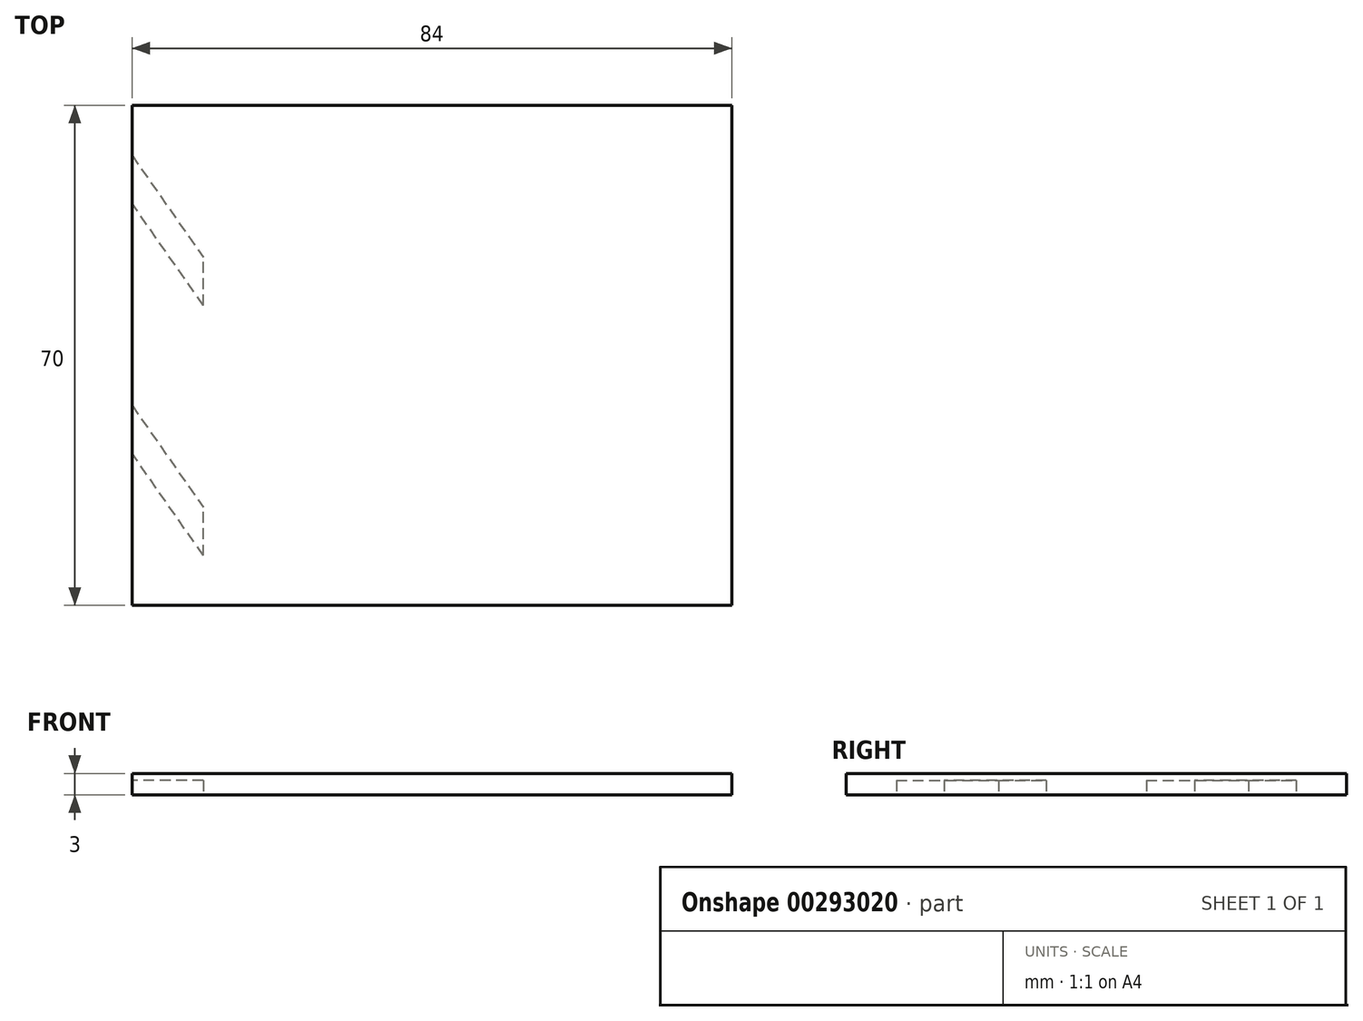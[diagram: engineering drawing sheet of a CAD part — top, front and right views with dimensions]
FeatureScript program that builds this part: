
annotation { "Feature Type Name" : "Feature", "Feature Type Description" : "" }
export const myFeature = defineFeature(function(context is Context, id is Id, definition is map)
    precondition{}
    {
        {
            var Q0;
            Q0=qCreatedBy(makeId("Front.planeOp"),FACE);
            var sketch = newSketch(context, id + "F0", { "sketchPlane" : qUnion([Q0])});
            skLineSegment(sketch, "E0.bottom", {"start": v(0, -23) * mm, "end": v(42, -23) * mm});
            skLineSegment(sketch, "E0.top", {"start": v(0, -20) * mm, "end": v(42, -20) * mm});
            skLineSegment(sketch, "E0.left", {"start": v(0, -23) * mm, "end": v(0, -20) * mm});
            skLineSegment(sketch, "E0.right", {"start": v(42, -23) * mm, "end": v(42, -20) * mm});
            skLineSegment(sketch, "E1", {"start": v(0, 0) * mm, "end": v(0, -20) * mm, "construction": true});
            skLineSegment(sketch, "E2", {"start": v(42, -21.5) * mm, "end": v(34, -21.5) * mm, "construction": true});
            skPoint(sketch, "E2.endSnap0", {"position": v(42, -21.5) * mm});
            skLineSegment(sketch, "E3", {"start": v(34, -21.5) * mm, "end": v(32, -21.5) * mm, "construction": true});
            skLineSegment(sketch, "E4", {"start": v(32, -21.5) * mm, "end": v(30, -21.5) * mm, "construction": true});
            skLineSegment(sketch, "E5", {"start": v(30, -21.5) * mm, "end": v(21, -21.5) * mm, "construction": true});
            skLineSegment(sketch, "E6", {"start": v(21, -21.5) * mm, "end": v(17, -21.5) * mm, "construction": true});
            skLineSegment(sketch, "E7", {"start": v(17, -21.5) * mm, "end": v(0, -21.5) * mm, "construction": true});
            skLineSegment(sketch, "E8", {"start": v(32, -21.5) * mm, "end": v(32, -23) * mm, "construction": true});
            skLineSegment(sketch, "E9", {"start": v(32, -23) * mm, "end": v(32, -21) * mm});
            skPoint(sketch, "E9.endSnap0", {"position": v(32, -22.25) * mm});
            skLineSegment(sketch, "E10", {"start": v(32, -21) * mm, "end": v(42, -21) * mm});
            skLineSegment(sketch, "E11", {"start": v(32, -22.25) * mm, "end": v(38, -22.25) * mm, "construction": true});
            skLineSegment(sketch, "E12", {"start": v(38, -22.25) * mm, "end": v(38, -23) * mm});
            skLineSegment(sketch, "E13", {"start": v(38, -23) * mm, "end": v(38, -21) * mm});
            skLineSegment(sketch, "E14.MirrorCS", {"start": v(-32, -23) * mm, "end": v(-32, -21) * mm});
            skLineSegment(sketch, "E15.MirrorCS", {"start": v(-32, -21.5) * mm, "end": v(-32, -23) * mm, "construction": true});
            skLineSegment(sketch, "E16.MirrorCS", {"start": v(-34, -21.5) * mm, "end": v(-32, -21.5) * mm, "construction": true});
            skLineSegment(sketch, "E17.MirrorCS", {"start": v(-32, -21.5) * mm, "end": v(-30, -21.5) * mm, "construction": true});
            skLineSegment(sketch, "E18.MirrorCS", {"start": v(-38, -23) * mm, "end": v(-38, -21) * mm});
            skLineSegment(sketch, "E19.MirrorCS", {"start": v(-38, -22.25) * mm, "end": v(-38, -23) * mm});
            skLineSegment(sketch, "E20.MirrorCS", {"start": v(-42, -23) * mm, "end": v(-42, -20) * mm});
            skLineSegment(sketch, "E21.MirrorCS", {"start": v(-42, -21.5) * mm, "end": v(-34, -21.5) * mm, "construction": true});
            skLineSegment(sketch, "E22.MirrorCS", {"start": v(-32, -21) * mm, "end": v(-42, -21) * mm});
            skLineSegment(sketch, "E23.MirrorCS", {"start": v(-32, -22.25) * mm, "end": v(-38, -22.25) * mm, "construction": true});
            skPoint(sketch, "E24.MirrorP", {"position": v(-42, -21.5) * mm});
            skLineSegment(sketch, "E25.MirrorCS", {"start": v(-30, -21.5) * mm, "end": v(-21, -21.5) * mm, "construction": true});
            skPoint(sketch, "E26.MirrorP", {"position": v(-32, -22.25) * mm});
            skLineSegment(sketch, "E27.MirrorCS", {"start": v(-21, -21.5) * mm, "end": v(-17, -21.5) * mm, "construction": true});
            skLineSegment(sketch, "E28.MirrorCS", {"start": v(-21, 40) * mm, "end": v(-17, 40) * mm});
            skLineSegment(sketch, "E29.MirrorCS", {"start": v(-30, 40) * mm, "end": v(-34, 40) * mm});
            skLineSegment(sketch, "E30.MirrorCS", {"start": v(0, -23) * mm, "end": v(-42, -23) * mm});
            skLineSegment(sketch, "E31.MirrorCS", {"start": v(-30, 40) * mm, "end": v(-30, -21.5) * mm});
            skLineSegment(sketch, "E32.MirrorCS", {"start": v(-17, 40) * mm, "end": v(-17, -21.5) * mm});
            skLineSegment(sketch, "E33.MirrorCS", {"start": v(-34, -21.5) * mm, "end": v(-34, 40) * mm});
            skLineSegment(sketch, "E34.MirrorCS", {"start": v(0, -20) * mm, "end": v(-42, -20) * mm});
            skLineSegment(sketch, "E35.MirrorCS", {"start": v(-17, -21.5) * mm, "end": v(0, -21.5) * mm, "construction": true});
            skLineSegment(sketch, "E36.MirrorCS", {"start": v(-21, -21.5) * mm, "end": v(-21, 40) * mm});
            skSolve(sketch);
        }
        {
            var Q0;
            {var subQ5=sQuery(id+"F0.wireOp",EDGE,"rBg3Q4IR-CGkZ-PO5m-HV7D-72pnYfLjL1so");Q0=makeQuery(id+"F0.imprint","IMPRINT",FACE,{"disambiguationData":[TD([[makeQuery(id+"F0.imprint","IMPRINT",EDGE,{"derivedFrom":subQ5}),1.0]])]});}
            var Q1;
            {var subQ5=sQuery(id+"F0.wireOp",EDGE,"dkqnGSy7-Vz6o-ykO8-f6sr-zODuD2kIRj3Q");Q1=makeQuery(id+"F0.imprint","IMPRINT",FACE,{"disambiguationData":[TD([[makeQuery(id+"F0.imprint","IMPRINT",EDGE,{"derivedFrom":subQ5}),-1.0]])]});}
            var Q2;
            {var subQ10=sQuery(id+"F0.wireOp",EDGE,"E9");Q2=makeQuery(id+"F0.imprint","IMPRINT",FACE,{"disambiguationData":[TD([[makeQuery(id+"F0.imprint","IMPRINT",EDGE,{"derivedFrom":subQ10}),1.0]])]});}
            var Q3;
            {var subQ1=sQuery(id+"F0.wireOp",EDGE,"E0.right");var subQ4=sQuery(id+"F0.wireOp",EDGE,"E0.top");var subQ5=makeQuery(id+"F0.imprint","INTERSECT",VERTEX,{"derivedFrom":[subQ4,subQ1]});Q3=makeQuery(id+"F0.imprint","IMPRINT",FACE,{"disambiguationData":[TD([[makeQuery(id+"F0.imprint","IMPRINT",EDGE,{"disambiguationData":[TD([[subQ5,1.0]])],"derivedFrom":subQ4}),-1.0]])]});}
            var Q4;
            {var subQ4=sQuery(id+"F0.wireOp",EDGE,"E9");Q4=makeQuery(id+"F0.imprint","IMPRINT",FACE,{"disambiguationData":[TD([[makeQuery(id+"F0.imprint","IMPRINT",EDGE,{"derivedFrom":subQ4}),-1.0]])]});}
            var Q5;
            {var subQ0=sQuery(id+"F0.wireOp",EDGE,"E13");var subQ3=makeQuery(id+"F0.imprint","IMPRINT",VERTEX,{"derivedFrom":subQ0});Q5=makeQuery(id+"F0.imprint","IMPRINT",FACE,{"disambiguationData":[TD([[makeQuery(id+"F0.imprint","IMPRINT",EDGE,{"disambiguationData":[TD([[subQ3,1.0]])],"derivedFrom":subQ0}),-1.0]])]});}
            var Q6;
            {var subQ6=sQuery(id+"F0.wireOp",EDGE,"E0.left");Q6=makeQuery(id+"F0.imprint","IMPRINT",FACE,{"disambiguationData":[TD([[makeQuery(id+"F0.imprint","IMPRINT",EDGE,{"derivedFrom":subQ6}),1.0]])]});}
            var Q7;
            {var subQ1=sQuery(id+"F0.wireOp",EDGE,"E22.MirrorCS");var subQ8=makeQuery(id+"F0.imprint","INTERSECT",VERTEX,{"derivedFrom":[sQuery(id+"F0.wireOp",EDGE,"E18.MirrorCS"),subQ1]});Q7=makeQuery(id+"F0.imprint","IMPRINT",FACE,{"disambiguationData":[TD([[makeQuery(id+"F0.imprint","IMPRINT",EDGE,{"disambiguationData":[TD([[subQ8,1.0]])],"derivedFrom":subQ1}),-1.0]])]});}
            var Q8;
            {var subQ1=sQuery(id+"F0.wireOp",EDGE,"E18.MirrorCS");var subQ5=makeQuery(id+"F0.imprint","IMPRINT",VERTEX,{"derivedFrom":subQ1});Q8=makeQuery(id+"F0.imprint","IMPRINT",FACE,{"disambiguationData":[TD([[makeQuery(id+"F0.imprint","IMPRINT",EDGE,{"disambiguationData":[TD([[subQ5,1.0]])],"derivedFrom":subQ1}),1.0]])]});}
            var Q9;
            {var subQ1=sQuery(id+"F0.wireOp",EDGE,"E14.MirrorCS");Q9=makeQuery(id+"F0.imprint","IMPRINT",FACE,{"disambiguationData":[TD([[makeQuery(id+"F0.imprint","IMPRINT",EDGE,{"derivedFrom":subQ1}),1.0]])]});}
            extrude(context, id + "F1", {"entities" : qUnion([Q0, Q1, Q2, Q3, Q4, Q5, Q6, Q7, Q8, Q9]), "depth" : 70 * mm});
        }
        {
            var Q0;
            Q0=makeQuery(id+"F1.opExtrude","SWEPT_FACE",FACE,{"disambiguationData":[OSD([sQuery(id+"F0.wireOp",EDGE,"E0.bottom"),sQuery(id+"F0.wireOp",EDGE,"E30.MirrorCS")])]});
            var sketch = newSketch(context, id + "F2", { "sketchPlane" : qUnion([Q0])});
            skLineSegment(sketch, "E37", {"start": v(42, 0) * mm, "end": v(-42, 0) * mm, "construction": true});
            skLineSegment(sketch, "E38", {"start": v(-42, 0) * mm, "end": v(-42, 70) * mm, "construction": true});
            skLineSegment(sketch, "E39", {"start": v(-42, 70) * mm, "end": v(42, 70) * mm, "construction": true});
            skLineSegment(sketch, "E40", {"start": v(0, 70) * mm, "end": v(0, 0) * mm});
            skLineSegment(sketch, "E41", {"start": v(42, 35) * mm, "end": v(42, 0) * mm, "construction": true});
            skLineSegment(sketch, "E42.MirrorCS", {"start": v(-42, 35) * mm, "end": v(42, 35) * mm});
            skLineSegment(sketch, "E43.MirrorCS", {"start": v(42, 35) * mm, "end": v(42, 70) * mm, "construction": true});
            skLineSegment(sketch, "E44", {"start": v(42, 70) * mm, "end": v(42, 0) * mm, "construction": true});
            skLineSegment(sketch, "E45", {"start": v(42, 70) * mm, "end": v(32, 70) * mm, "construction": true});
            skLineSegment(sketch, "E46", {"start": v(32, 70) * mm, "end": v(32, 35) * mm, "construction": true});
            skLineSegment(sketch, "E47", {"start": v(32, 35) * mm, "end": v(42, 35) * mm, "construction": true});
            skLineSegment(sketch, "E48", {"start": v(42, 42) * mm, "end": v(32, 56.28) * mm});
            skLineSegment(sketch, "E49", {"start": v(32, 56.28) * mm, "end": v(32, 63) * mm});
            skLineSegment(sketch, "E50", {"start": v(32, 63) * mm, "end": v(42, 48.72) * mm});
            skLineSegment(sketch, "E51", {"start": v(42, 48.72) * mm, "end": v(42, 42) * mm});
            skLineSegment(sketch, "E52.MirrorCS", {"start": v(-32, 63) * mm, "end": v(-42, 48.72) * mm});
            skLineSegment(sketch, "E53.MirrorCS", {"start": v(-42, 42) * mm, "end": v(-32, 56.28) * mm});
            skLineSegment(sketch, "E54.MirrorCS", {"start": v(-32, 70) * mm, "end": v(-32, 35) * mm, "construction": true});
            skLineSegment(sketch, "E55", {"start": v(-32, 63) * mm, "end": v(-32, 56.28) * mm});
            skLineSegment(sketch, "E56", {"start": v(-42, 48.72) * mm, "end": v(-42, 42) * mm});
            skLineSegment(sketch, "E57", {"start": v(-42, 0) * mm, "end": v(-42, 7) * mm, "construction": true});
            skLineSegment(sketch, "E58", {"start": v(42, 0) * mm, "end": v(42, 7) * mm, "construction": true});
            skLineSegment(sketch, "E59.MirrorCS", {"start": v(-32, 0) * mm, "end": v(-32, 35) * mm, "construction": true});
            skLineSegment(sketch, "E60", {"start": v(32, 35) * mm, "end": v(32, 0) * mm, "construction": true});
            skLineSegment(sketch, "E61", {"start": v(32, 35) * mm, "end": v(32, 28) * mm, "construction": true});
            skLineSegment(sketch, "E62", {"start": v(-32, 35) * mm, "end": v(-32, 28) * mm, "construction": true});
            skLineSegment(sketch, "E63", {"start": v(-42, 7) * mm, "end": v(-32, 21.28) * mm});
            skLineSegment(sketch, "E64", {"start": v(42, 7) * mm, "end": v(32, 21.28) * mm});
            skLineSegment(sketch, "E65", {"start": v(-32, 28) * mm, "end": v(-42, 13.72) * mm});
            skLineSegment(sketch, "E66", {"start": v(32, 28) * mm, "end": v(42, 13.72) * mm});
            skLineSegment(sketch, "E67", {"start": v(42, 13.72) * mm, "end": v(42, 7) * mm});
            skLineSegment(sketch, "E68", {"start": v(32, 21.28) * mm, "end": v(32, 28) * mm});
            skLineSegment(sketch, "E69", {"start": v(-42, 13.72) * mm, "end": v(-42, 7) * mm});
            skLineSegment(sketch, "E70", {"start": v(-32, 28) * mm, "end": v(-32, 21.28) * mm});
            skLineSegment(sketch, "E71", {"start": v(42, 7) * mm, "end": v(42, 13.72) * mm});
            skLineSegment(sketch, "E72", {"start": v(-42, 7) * mm, "end": v(-42, 13.72) * mm});
            skLineSegment(sketch, "E73", {"start": v(-42, 42) * mm, "end": v(-42, 48.72) * mm});
            skSolve(sketch);
        }
        {
            var Q0;
            Q0=makeQuery(id+"F2.imprint","IMPRINT",FACE,{"disambiguationData":[TD([[makeQuery(id+"F2.imprint","IMPRINT",EDGE,{"derivedFrom":sQuery(id+"F2.wireOp",EDGE,"E63")}),1.0]])]});
            var Q1;
            Q1=makeQuery(id+"F2.imprint","IMPRINT",FACE,{"disambiguationData":[TD([[makeQuery(id+"F2.imprint","IMPRINT",EDGE,{"derivedFrom":sQuery(id+"F2.wireOp",EDGE,"E52.MirrorCS")}),1.0]])]});
            extrude(context, id + "F3", {"entities" : qUnion([Q0, Q1]), "operationType" : NewBodyOperationType.REMOVE, "oppositeDirection" : true, "depth" : 2 * mm});
        }
    });
